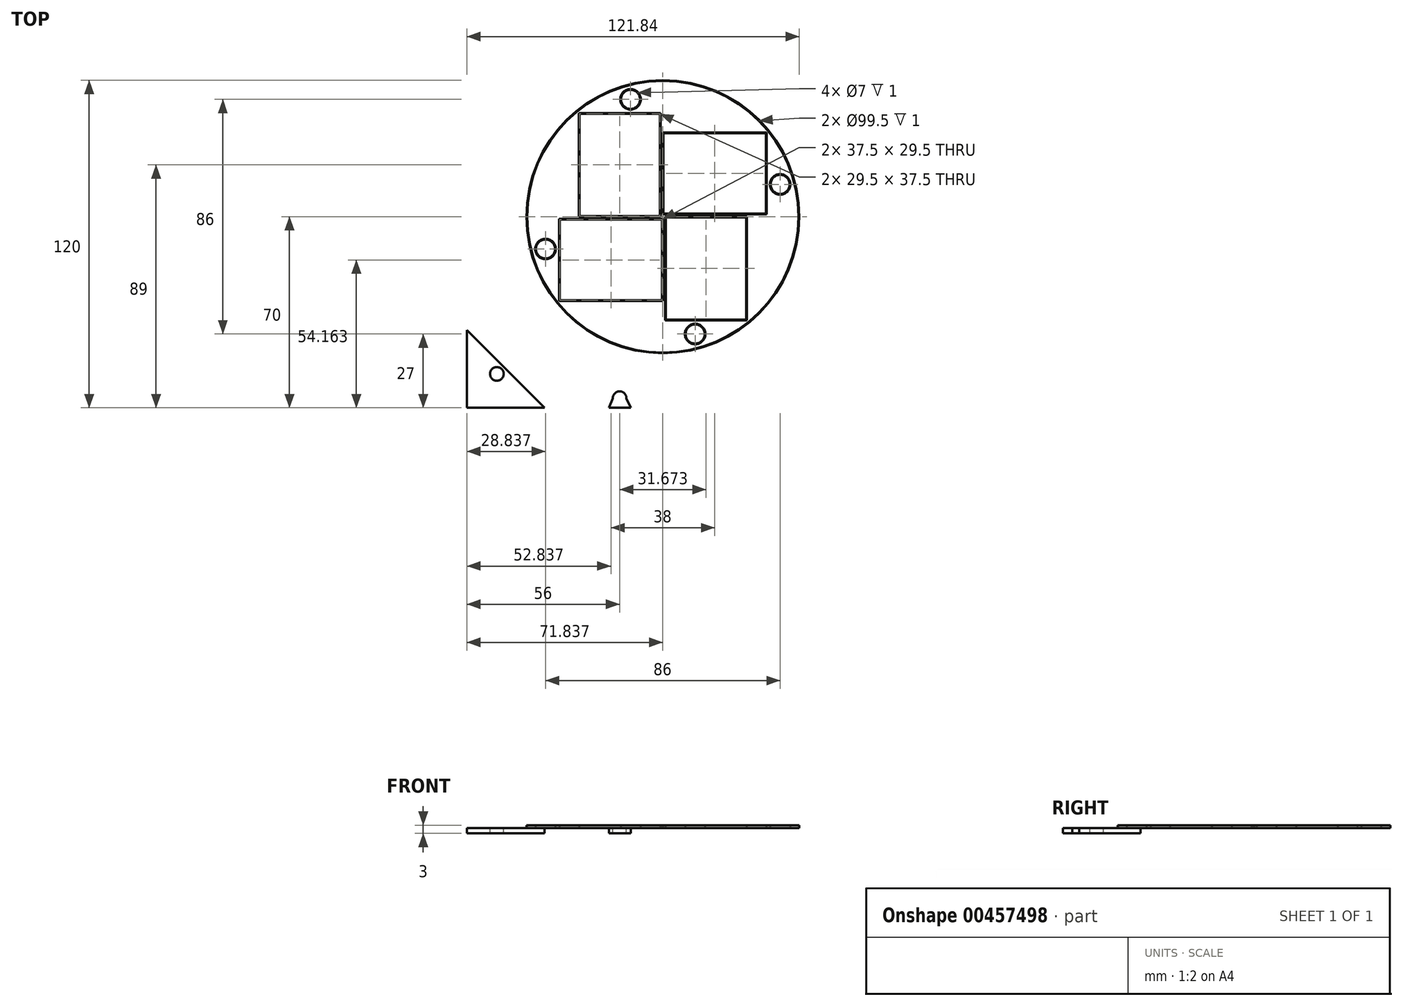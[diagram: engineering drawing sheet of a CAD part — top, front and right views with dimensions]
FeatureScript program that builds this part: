
annotation { "Feature Type Name" : "Feature", "Feature Type Description" : "" }
export const myFeature = defineFeature(function(context is Context, id is Id, definition is map)
    precondition{}
    {
        {
            var Q0;
            Q0=qCreatedBy(makeId("Top.planeOp"),FACE);
            var sketch = newSketch(context, id + "F0", { "sketchPlane" : qUnion([Q0])});
            skLineSegment(sketch, "E0.bottom", {"start": v(75, 70) * mm, "end": v(-75, 70) * mm});
            skLineSegment(sketch, "E0.top", {"start": v(75, -70) * mm, "end": v(-75, -70) * mm});
            skLineSegment(sketch, "E0.left", {"start": v(75, 70) * mm, "end": v(75, -70) * mm});
            skLineSegment(sketch, "E0.right", {"start": v(-75, 70) * mm, "end": v(-75, -70) * mm});
            skPoint(sketch, "E0.middle", {"position": v(0, 0) * mm});
            skSolve(sketch);
        }
        {
            var Q0;
            Q0=qSketchRegion(id+"F0",true);
            extrude(context, id + "F1", {"entities" : qUnion([Q0]), "depth" : 2 * mm});
        }
        {
            var Q0;
            Q0=makeQuery(id+"F1.opExtrude","CAP_FACE",FACE,{"disambiguationData":[OSD([sQuery(id+"F0.wireOp",EDGE,"E0.bottom"),sQuery(id+"F0.wireOp",EDGE,"E0.top"),sQuery(id+"F0.wireOp",EDGE,"E0.left"),sQuery(id+"F0.wireOp",EDGE,"E0.right")])],"isStart":false});
            var sketch = newSketch(context, id + "F2", { "sketchPlane" : qUnion([Q0])});
            skArc(sketch, "E1", {"start": v(-67.18, 6.35) * mm, "mid": v(-67.92, 8.12) * mm, "end": v(-69.68, 8.85) * mm});
            skArc(sketch, "E2.MirrorC", {"start": v(-67.18, -6.35) * mm, "mid": v(-67.92, -8.12) * mm, "end": v(-69.68, -8.85) * mm});
            skArc(sketch, "E3", {"start": v(-21.5, 66.52) * mm, "mid": v(-19, 64) * mm, "end": v(-16.5, 66.52) * mm});
            skCircle(sketch, "E4", {"center": v(-64, 57.6) * mm, "radius": 2.5 * mm});
            skArc(sketch, "E5.MirrorC", {"start": v(-21.5, -66.52) * mm, "mid": v(-19, -64) * mm, "end": v(-16.5, -66.52) * mm});
            skCircle(sketch, "E6.MirrorC", {"center": v(-64, -57.6) * mm, "radius": 2.5 * mm});
            skLineSegment(sketch, "E7", {"start": v(-21.5, 66.52) * mm, "end": v(-22.94, 70) * mm});
            skLineSegment(sketch, "E8.MirrorCS", {"start": v(-16.5, 66.52) * mm, "end": v(-14.88, 70) * mm});
            skLineSegment(sketch, "E9.MirrorCS", {"start": v(-16.5, -66.52) * mm, "end": v(-14.88, -70) * mm});
            skLineSegment(sketch, "E10.MirrorCS", {"start": v(-21.5, -66.52) * mm, "end": v(-22.94, -70) * mm});
            skLineSegment(sketch, "E11", {"start": v(-46.5, 70) * mm, "end": v(-75, 41.5) * mm});
            skLineSegment(sketch, "E12.MirrorCS", {"start": v(-46.5, -70) * mm, "end": v(-75, -41.5) * mm});
            skLineSegment(sketch, "E13", {"start": v(-69.68, 8.85) * mm, "end": v(-75, 8.85) * mm});
            skLineSegment(sketch, "E14", {"start": v(-67.18, -6.35) * mm, "end": v(-67.18, 6.35) * mm});
            skLineSegment(sketch, "E15.MirrorCS", {"start": v(-69.68, -8.85) * mm, "end": v(-75, -8.85) * mm});
            skSolve(sketch);
        }
        {
            var Q0;
            Q0=qSketchRegion(id+"F2",true);
            var Q1;
            Q1=makeQuery(id+"F2.imprint","IMPRINT",FACE,{"disambiguationData":[TD([[makeQuery(id+"F2.imprint","IMPRINT",EDGE,{"derivedFrom":sQuery(id+"F2.wireOp",EDGE,"E4")}),-1.0]])]});
            var Q2;
            Q2=makeQuery(id+"F2.imprint","IMPRINT",FACE,{"disambiguationData":[TD([[makeQuery(id+"F2.imprint","IMPRINT",EDGE,{"derivedFrom":sQuery(id+"F2.wireOp",EDGE,"E1")}),1.0]])]});
            var Q3;
            Q3=makeQuery(id+"F2.imprint","IMPRINT",FACE,{"disambiguationData":[TD([[makeQuery(id+"F2.imprint","IMPRINT",EDGE,{"derivedFrom":sQuery(id+"F2.wireOp",EDGE,"E5.MirrorC")}),-1.0]])]});
            var Q4;
            Q4=makeQuery(id+"F2.imprint","IMPRINT",FACE,{"disambiguationData":[TD([[makeQuery(id+"F2.imprint","IMPRINT",EDGE,{"derivedFrom":sQuery(id+"F2.wireOp",EDGE,"E3")}),1.0]])]});
            var Q5;
            Q5=makeQuery(id+"F2.imprint","IMPRINT",FACE,{"disambiguationData":[TD([[makeQuery(id+"F2.imprint","IMPRINT",EDGE,{"derivedFrom":sQuery(id+"F2.wireOp",EDGE,"E6.MirrorC")}),1.0]])]});
            extrude(context, id + "F3", {"entities" : qUnion([Q0, Q1, Q2, Q3, Q4, Q5]), "operationType" : NewBodyOperationType.REMOVE, "oppositeDirection" : true, "depth" : 5 * mm});
        }
        {
            var Q0;
            Q0=makeQuery(id+"F1.opExtrude","CAP_FACE",FACE,{"disambiguationData":[OSD([sQuery(id+"F0.wireOp",EDGE,"E0.bottom"),sQuery(id+"F0.wireOp",EDGE,"E0.top"),sQuery(id+"F0.wireOp",EDGE,"E0.left"),sQuery(id+"F0.wireOp",EDGE,"E0.right")])],"isStart":false});
            var sketch = newSketch(context, id + "F4", { "sketchPlane" : qUnion([Q0])});
            skCircle(sketch, "E16", {"center": v(-3.16, 0) * mm, "radius": 50 * mm});
            skCircle(sketch, "E17", {"center": v(-3.16, 0) * mm, "radius": 49.5 * mm});
            skCircle(sketch, "E18", {"center": v(-3.16, 0) * mm, "radius": 49.75 * mm});
            skLineSegment(sketch, "E19.bottom", {"start": v(-4, 38) * mm, "end": v(-34, 38) * mm});
            skLineSegment(sketch, "E19.top", {"start": v(-4, 0) * mm, "end": v(-34, 0) * mm});
            skLineSegment(sketch, "E19.left", {"start": v(-4, 38) * mm, "end": v(-4, 0) * mm});
            skLineSegment(sketch, "E19.right", {"start": v(-34, 38) * mm, "end": v(-34, 0) * mm});
            skPoint(sketch, "E19.middle", {"position": v(-19, 19) * mm});
            skLineSegment(sketch, "E20.bottom", {"start": v(-4.25, 37.75) * mm, "end": v(-33.75, 37.75) * mm});
            skLineSegment(sketch, "E20.top", {"start": v(-4.25, 0.25) * mm, "end": v(-33.75, 0.25) * mm});
            skLineSegment(sketch, "E20.left", {"start": v(-4.25, 37.75) * mm, "end": v(-4.25, 0.25) * mm});
            skLineSegment(sketch, "E20.right", {"start": v(-33.75, 37.75) * mm, "end": v(-33.75, 0.25) * mm});
            skCircle(sketch, "E21", {"center": v(-15, 43) * mm, "radius": 3.75 * mm});
            skCircle(sketch, "E22", {"center": v(-15, 43) * mm, "radius": 3.5 * mm});
            skLineSegment(sketch, "E23.1.0", {"start": v(-41.16, -0.84) * mm, "end": v(-3.16, -0.84) * mm});
            skLineSegment(sketch, "E23.1.1", {"start": v(-40.91, -1.09) * mm, "end": v(-3.41, -1.09) * mm});
            skLineSegment(sketch, "E23.1.2", {"start": v(-40.91, -1.09) * mm, "end": v(-40.91, -30.59) * mm});
            skLineSegment(sketch, "E23.1.3", {"start": v(-41.16, -0.84) * mm, "end": v(-41.16, -30.84) * mm});
            skLineSegment(sketch, "E23.1.4", {"start": v(-40.91, -30.59) * mm, "end": v(-3.41, -30.59) * mm});
            skLineSegment(sketch, "E23.1.5", {"start": v(-41.16, -30.84) * mm, "end": v(-3.16, -30.84) * mm});
            skLineSegment(sketch, "E23.1.6", {"start": v(-3.16, -0.84) * mm, "end": v(-3.16, -30.84) * mm});
            skLineSegment(sketch, "E23.1.7", {"start": v(-3.41, -1.09) * mm, "end": v(-3.41, -30.59) * mm});
            skCircle(sketch, "E23.1.8", {"center": v(-46.16, -11.84) * mm, "radius": 3.5 * mm});
            skCircle(sketch, "E23.1.9", {"center": v(-46.16, -11.84) * mm, "radius": 3.75 * mm});
            skLineSegment(sketch, "E23.2.0", {"start": v(-2.33, -38) * mm, "end": v(-2.33, 0) * mm});
            skLineSegment(sketch, "E23.2.1", {"start": v(-2.08, -37.75) * mm, "end": v(-2.08, -0.25) * mm});
            skLineSegment(sketch, "E23.2.2", {"start": v(-2.08, -37.75) * mm, "end": v(27.42, -37.75) * mm});
            skLineSegment(sketch, "E23.2.3", {"start": v(-2.33, -38) * mm, "end": v(27.67, -38) * mm});
            skLineSegment(sketch, "E23.2.4", {"start": v(27.42, -37.75) * mm, "end": v(27.42, -0.25) * mm});
            skLineSegment(sketch, "E23.2.5", {"start": v(27.67, -38) * mm, "end": v(27.67, 0) * mm});
            skLineSegment(sketch, "E23.2.6", {"start": v(-2.33, 0) * mm, "end": v(27.67, 0) * mm});
            skLineSegment(sketch, "E23.2.7", {"start": v(-2.08, -0.25) * mm, "end": v(27.42, -0.25) * mm});
            skCircle(sketch, "E23.2.8", {"center": v(8.67, -43) * mm, "radius": 3.5 * mm});
            skCircle(sketch, "E23.2.9", {"center": v(8.67, -43) * mm, "radius": 3.75 * mm});
            skLineSegment(sketch, "E23.3.0", {"start": v(34.84, 0.84) * mm, "end": v(-3.16, 0.84) * mm});
            skLineSegment(sketch, "E23.3.1", {"start": v(34.59, 1.09) * mm, "end": v(-2.91, 1.09) * mm});
            skLineSegment(sketch, "E23.3.2", {"start": v(34.59, 1.09) * mm, "end": v(34.59, 30.59) * mm});
            skLineSegment(sketch, "E23.3.3", {"start": v(34.84, 0.84) * mm, "end": v(34.84, 30.84) * mm});
            skLineSegment(sketch, "E23.3.4", {"start": v(34.59, 30.59) * mm, "end": v(-2.91, 30.59) * mm});
            skLineSegment(sketch, "E23.3.5", {"start": v(34.84, 30.84) * mm, "end": v(-3.16, 30.84) * mm});
            skLineSegment(sketch, "E23.3.6", {"start": v(-3.16, 0.84) * mm, "end": v(-3.16, 30.84) * mm});
            skLineSegment(sketch, "E23.3.7", {"start": v(-2.91, 1.09) * mm, "end": v(-2.91, 30.59) * mm});
            skCircle(sketch, "E23.3.8", {"center": v(39.84, 11.84) * mm, "radius": 3.5 * mm});
            skCircle(sketch, "E23.3.9", {"center": v(39.84, 11.84) * mm, "radius": 3.75 * mm});
            skSolve(sketch);
        }
        {
            var Q0;
            Q0=qSketchRegion(id+"F4",true);
            var Q1;
            Q1=makeQuery(id+"F4.imprint","IMPRINT",FACE,{"disambiguationData":[TD([[makeQuery(id+"F4.imprint","IMPRINT",EDGE,{"derivedFrom":sQuery(id+"F4.wireOp",EDGE,"pkoXZPiR-0mkQ-UggU-QeDQ-18WsZVd6IxUX")}),1.0]])]});
            var Q2;
            Q2=makeQuery(id+"F4.imprint","IMPRINT",FACE,{"disambiguationData":[TD([[makeQuery(id+"F4.imprint","IMPRINT",EDGE,{"derivedFrom":sQuery(id+"F4.wireOp",EDGE,"K1UoebT6-E9hS-h827-5MM4-wNKjuZ17nWzt.bottom")}),-1.0]])]});
            var Q3;
            Q3=makeQuery(id+"F4.imprint","IMPRINT",FACE,{"disambiguationData":[TD([[makeQuery(id+"F4.imprint","IMPRINT",EDGE,{"derivedFrom":sQuery(id+"F4.wireOp",EDGE,"6895091a-fd66-4955-bf57-3f23905b837a.3.0")}),1.0]])]});
            var Q4;
            Q4=makeQuery(id+"F4.imprint","IMPRINT",FACE,{"disambiguationData":[TD([[makeQuery(id+"F4.imprint","IMPRINT",EDGE,{"derivedFrom":sQuery(id+"F4.wireOp",EDGE,"2bf1c8c4-409d-43ad-88c8-fcb9e33b7025.3.0")}),1.0]])]});
            var Q5;
            Q5=makeQuery(id+"F4.imprint","IMPRINT",FACE,{"disambiguationData":[TD([[makeQuery(id+"F4.imprint","IMPRINT",EDGE,{"derivedFrom":sQuery(id+"F4.wireOp",EDGE,"6895091a-fd66-4955-bf57-3f23905b837a.2.0")}),1.0]])]});
            var Q6;
            Q6=makeQuery(id+"F4.imprint","IMPRINT",FACE,{"disambiguationData":[TD([[makeQuery(id+"F4.imprint","IMPRINT",EDGE,{"derivedFrom":sQuery(id+"F4.wireOp",EDGE,"2bf1c8c4-409d-43ad-88c8-fcb9e33b7025.2.0")}),1.0]])]});
            var Q7;
            Q7=makeQuery(id+"F4.imprint","IMPRINT",FACE,{"disambiguationData":[TD([[makeQuery(id+"F4.imprint","IMPRINT",EDGE,{"derivedFrom":sQuery(id+"F4.wireOp",EDGE,"6895091a-fd66-4955-bf57-3f23905b837a.1.0")}),1.0]])]});
            var Q8;
            Q8=makeQuery(id+"F4.imprint","IMPRINT",FACE,{"disambiguationData":[TD([[makeQuery(id+"F4.imprint","IMPRINT",EDGE,{"derivedFrom":sQuery(id+"F4.wireOp",EDGE,"2bf1c8c4-409d-43ad-88c8-fcb9e33b7025.1.0")}),1.0]])]});
            extrude(context, id + "F5", {"entities" : qUnion([Q0, Q1, Q2, Q3, Q4, Q5, Q6, Q7, Q8]), "depth" : 1 * mm});
        }
        {
            var Q0;
            Q0=qSketchRegion(id+"F4",true);
            var Q1;
            Q1=makeQuery(id+"F4.imprint","IMPRINT",FACE,{"disambiguationData":[TD([[makeQuery(id+"F4.imprint","IMPRINT",EDGE,{"derivedFrom":sQuery(id+"F4.wireOp",EDGE,"E23.1.0")}),-1.0]])]});
            var Q2;
            Q2=makeQuery(id+"F4.imprint","IMPRINT",FACE,{"disambiguationData":[TD([[makeQuery(id+"F4.imprint","IMPRINT",EDGE,{"derivedFrom":sQuery(id+"F4.wireOp",EDGE,"E23.1.8")}),-1.0]])]});
            var Q3;
            Q3=makeQuery(id+"F4.imprint","IMPRINT",FACE,{"disambiguationData":[TD([[makeQuery(id+"F4.imprint","IMPRINT",EDGE,{"derivedFrom":sQuery(id+"F4.wireOp",EDGE,"E19.bottom")}),1.0]])]});
            var Q4;
            Q4=makeQuery(id+"F4.imprint","IMPRINT",FACE,{"disambiguationData":[TD([[makeQuery(id+"F4.imprint","IMPRINT",EDGE,{"derivedFrom":sQuery(id+"F4.wireOp",EDGE,"E23.3.0")}),-1.0]])]});
            var Q5;
            Q5=makeQuery(id+"F4.imprint","IMPRINT",FACE,{"disambiguationData":[TD([[makeQuery(id+"F4.imprint","IMPRINT",EDGE,{"derivedFrom":sQuery(id+"F4.wireOp",EDGE,"E23.2.0")}),-1.0]])]});
            var Q6;
            Q6=makeQuery(id+"F4.imprint","IMPRINT",FACE,{"disambiguationData":[TD([[makeQuery(id+"F4.imprint","IMPRINT",EDGE,{"derivedFrom":sQuery(id+"F4.wireOp",EDGE,"E23.3.8")}),-1.0]])]});
            var Q7;
            Q7=makeQuery(id+"F4.imprint","IMPRINT",FACE,{"disambiguationData":[TD([[makeQuery(id+"F4.imprint","IMPRINT",EDGE,{"derivedFrom":sQuery(id+"F4.wireOp",EDGE,"E23.2.8")}),-1.0]])]});
            var Q8;
            Q8=makeQuery(id+"F4.imprint","IMPRINT",FACE,{"disambiguationData":[TD([[makeQuery(id+"F4.imprint","IMPRINT",EDGE,{"derivedFrom":sQuery(id+"F4.wireOp",EDGE,"E21")}),1.0]])]});
            extrude(context, id + "F6", {"entities" : qUnion([Q0, Q1, Q2, Q3, Q4, Q5, Q6, Q7, Q8]), "depth" : 1 * mm});
        }
    });
